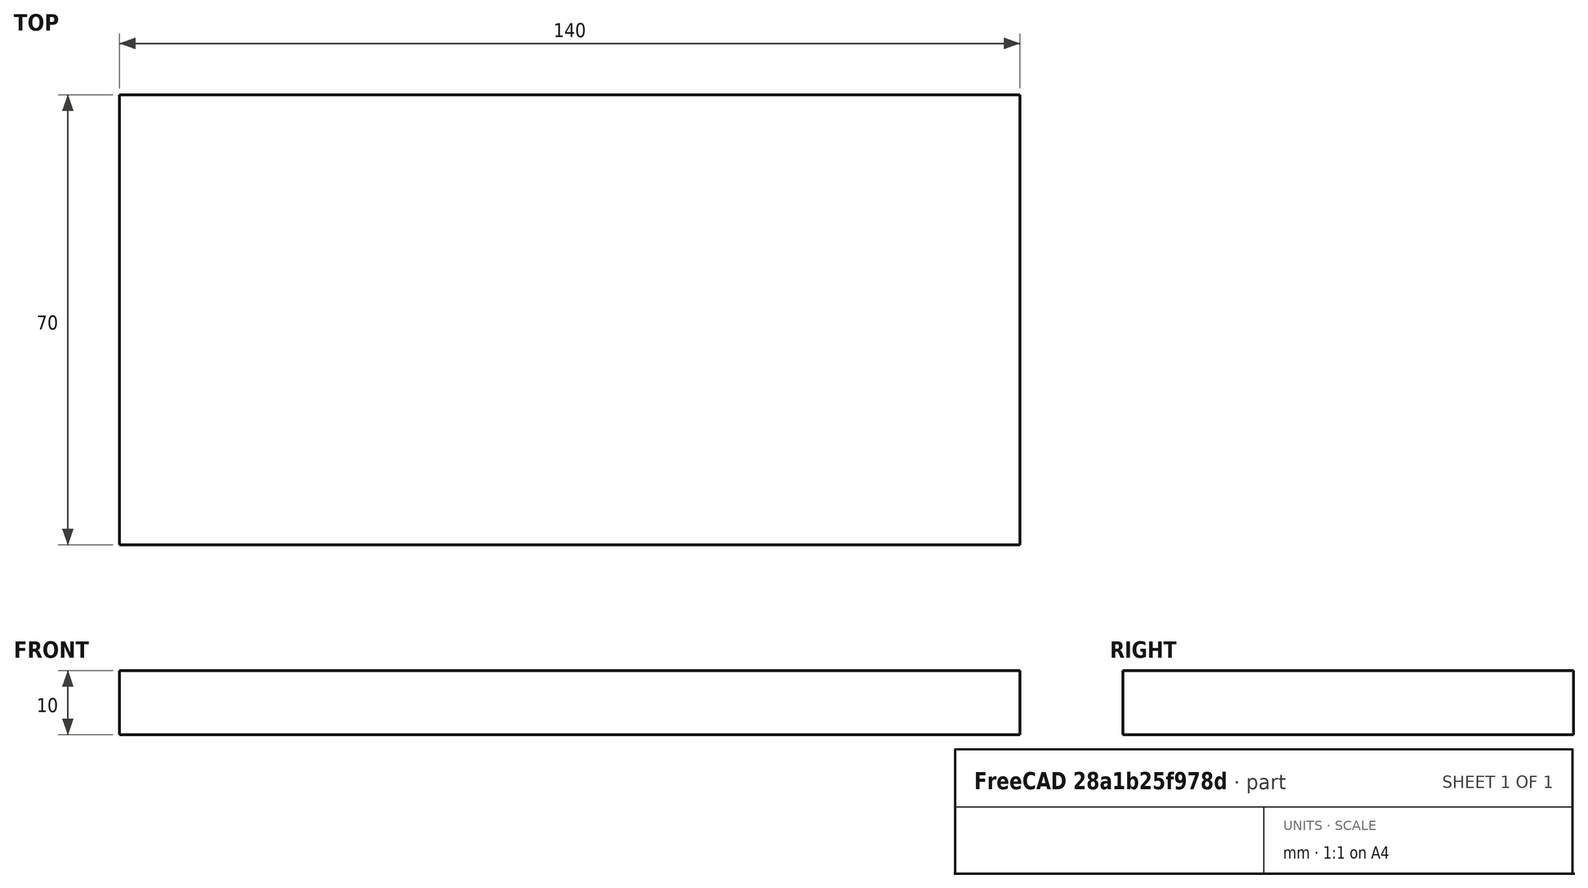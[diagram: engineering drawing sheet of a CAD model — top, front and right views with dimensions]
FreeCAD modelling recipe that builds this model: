
FCSTD DOCUMENT  (FreeCAD 0.18R16093 (Git))
Label: sidePanelRight
License: All rights reserved
LicenseURL: http://en.wikipedia.org/wiki/All_rights_reserved
objects: PartDesign::Fillet×4, Sketcher::SketchObject×3, Path::FeaturePython×3, PartDesign::Pocket×2, Part::FeaturePython×2, PartDesign::Pad×1, PartDesign::Body×1, App::FeaturePython×1, App::DocumentObjectGroup×1, Path::FeatureCompoundPython×1, Mesh::FeaturePython×1
note: 17 computed .brp shape members not serialized (recipe doc carries the construction recipe); baked Part::Feature solids carry a one-line shape summary decoded from their .brp

FEATURE [Sketcher::SketchObject] Sketch
  MapMode = 5
  Placement = pos=(0,0,0) rot=(0.57735,0.57735,0.57735;2.0944rad)
  Support = -> [YZ_Plane]
  sketch-geometry (4):
    g0: LineSegment StartX=-35 StartY=70 StartZ=0 EndX=35 EndY=70 EndZ=0
    g1: LineSegment StartX=35 StartY=70 StartZ=0 EndX=35 EndY=-70 EndZ=0
    g2: LineSegment StartX=35 StartY=-70 StartZ=0 EndX=-35 EndY=-70 EndZ=0
    g3: LineSegment StartX=-35 StartY=-70 StartZ=0 EndX=-35 EndY=70 EndZ=0
  constraints (10):
    c: Coincident(g0,g1)
    c: Coincident(g1,g2)
    c: Coincident(g2,g3)
    c: Coincident(g3,g0)
    c: DistanceY(g3,g3) = 140
    c: DistanceX(g0,g0) = 70
    c: Symmetric(g0,g0,g-2)
    c: Symmetric(g0,g2,g-1)
    c: Parallel(g3,g1)
    c: Parallel(g0,g2)
FEATURE [PartDesign::Pad] Pad
  Length = 10
  Length2 = 100
  Placement = pos=(0,0,0) rot=(0.57735,0.57735,0.57735;2.0944rad)
  Profile = -> Sketch
  Type = 0
FEATURE [PartDesign::Fillet] Fillet
  Base = -> Pad [Edge4]
  BaseFeature = -> Pad
  Placement = pos=(0,0,0) rot=(0.57735,0.57735,0.57735;2.0944rad)
  Radius = 3
FEATURE [PartDesign::Fillet] Fillet001
  Base = -> Fillet [Edge15]
  BaseFeature = -> Fillet
  Placement = pos=(0,0,0) rot=(0.57735,0.57735,0.57735;2.0944rad)
  Radius = 3
FEATURE [Sketcher::SketchObject] Sketch001
  MapMode = 5
  Placement = pos=(0,0,0) rot=(0.57735,0.57735,-0.57735;4.18879rad)
  Support = -> [Fillet001]
  sketch-geometry (24):
    g0: LineSegment StartX=-25 StartY=70 StartZ=0 EndX=-15 EndY=70 EndZ=0
    g1: LineSegment StartX=-15 StartY=70 StartZ=0 EndX=-15 EndY=60 EndZ=0
    g2: LineSegment StartX=-15 StartY=60 StartZ=0 EndX=-25 EndY=60 EndZ=0
    g3: LineSegment StartX=-25 StartY=60 StartZ=0 EndX=-25 EndY=70 EndZ=0
    g4: LineSegment StartX=-5 StartY=70 StartZ=0 EndX=5 EndY=70 EndZ=0
    g5: LineSegment StartX=5 StartY=70 StartZ=0 EndX=5 EndY=60 EndZ=0
    g6: LineSegment StartX=5 StartY=60 StartZ=0 EndX=-5 EndY=60 EndZ=0
    g7: LineSegment StartX=-5 StartY=60 StartZ=0 EndX=-5 EndY=70 EndZ=0
    g8: LineSegment StartX=25 StartY=70 StartZ=0 EndX=15 EndY=70 EndZ=0
    g9: LineSegment StartX=15 StartY=70 StartZ=0 EndX=15 EndY=60 EndZ=0
    g10: LineSegment StartX=15 StartY=60 StartZ=0 EndX=25 EndY=60 EndZ=0
    g11: LineSegment StartX=25 StartY=60 StartZ=0 EndX=25 EndY=70 EndZ=0
    g12: LineSegment StartX=-25 StartY=-70 StartZ=0 EndX=-15 EndY=-70 EndZ=0
    g13: LineSegment StartX=-15 StartY=-70 StartZ=0 EndX=-15 EndY=-60 EndZ=0
    g14: LineSegment StartX=-15 StartY=-60 StartZ=0 EndX=-25 EndY=-60 EndZ=0
    g15: LineSegment StartX=-25 StartY=-60 StartZ=0 EndX=-25 EndY=-70 EndZ=0
    g16: LineSegment StartX=-5 StartY=-70 StartZ=0 EndX=5 EndY=-70 EndZ=0
    g17: LineSegment StartX=5 StartY=-70 StartZ=0 EndX=5 EndY=-60 EndZ=0
    g18: LineSegment StartX=5 StartY=-60 StartZ=0 EndX=-5 EndY=-60 EndZ=0
    g19: LineSegment StartX=-5 StartY=-60 StartZ=0 EndX=-5 EndY=-70 EndZ=0
    g20: LineSegment StartX=25 StartY=-70 StartZ=0 EndX=15 EndY=-70 EndZ=0
    g21: LineSegment StartX=15 StartY=-70 StartZ=0 EndX=15 EndY=-60 EndZ=0
    g22: LineSegment StartX=15 StartY=-60 StartZ=0 EndX=25 EndY=-60 EndZ=0
    g23: LineSegment StartX=25 StartY=-60 StartZ=0 EndX=25 EndY=-70 EndZ=0
  constraints (70):
    c: Coincident(g0,g1)
    c: Coincident(g1,g2)
    c: Coincident(g2,g3)
    c: Coincident(g3,g0)
    c: Horizontal(g0)
    c: Horizontal(g2)
    c: Vertical(g1)
    c: Vertical(g3)
    c: DistanceX(g0,g0) = 10
    c: DistanceY(g2,g0) = 10
    c: DistanceY(g-1,g2) = 60
    c: Coincident(g4,g5)
    c: Coincident(g5,g6)
    c: Coincident(g6,g7)
    c: Coincident(g7,g4)
    c: Horizontal(g6)
    c: Vertical(g5)
    c: Vertical(g7)
    c: DistanceX(g0,g4) = 10
    c: DistanceX(g4,g4) = 10
    c: Horizontal(g6,g1)
    c: Horizontal(g4,g0)
    c: Coincident(g8,g9)
    c: Coincident(g9,g10)
    c: Coincident(g10,g11)
    c: Coincident(g11,g8)
    c: Horizontal(g8)
    c: Horizontal(g10)
    c: Vertical(g9)
    c: Vertical(g11)
    c: Horizontal(g5,g9)
    c: Horizontal(g4,g8)
    c: DistanceX(g4,g8) = 10
    c: DistanceX(g8,g8) = 10
    c: Coincident(g12,g13)
    c: Coincident(g13,g14)
    c: Coincident(g14,g15)
    c: Coincident(g15,g12)
    c: Horizontal(g12)
    c: Horizontal(g14)
    c: Vertical(g13)
    c: Vertical(g15)
    c: Coincident(g16,g17)
    c: Coincident(g17,g18)
    c: Coincident(g18,g19)
    c: Coincident(g19,g16)
    c: Horizontal(g16)
    c: Vertical(g17)
    c: Vertical(g19)
    c: Coincident(g20,g21)
    c: Coincident(g21,g22)
    c: Coincident(g22,g23)
    c: Coincident(g23,g20)
    c: Horizontal(g20)
    c: Horizontal(g22)
    c: Vertical(g21)
    c: Vertical(g23)
    c: DistanceY(g14,g-1) = 60
    c: DistanceY(g12,g14) = 10
    c: Horizontal(g13,g18)
    c: Horizontal(g17,g21)
    c: Horizontal(g12,g16)
    c: Horizontal(g16,g20)
    c: DistanceX(g12,g12) = 10
    c: DistanceX(g12,g16) = 10
    c: DistanceX(g16,g16) = 10
    c: DistanceX(g16,g20) = 10
    c: DistanceX(g20,g20) = 10
    c: Symmetric(g18,g17,g-2)
    c: Symmetric(g4,g4,g-2)
FEATURE [PartDesign::Pocket] Pocket
  BaseFeature = -> Fillet001
  Length = 5
  Length2 = 100
  Placement = pos=(0,0,0) rot=(0.57735,0.57735,0.57735;2.0944rad)
  Profile = -> Sketch001
  Type = 1
FEATURE [Sketcher::SketchObject] Sketch002
  MapMode = 5
  Placement = pos=(0,0,0) rot=(0.57735,0.57735,-0.57735;4.18879rad)
  Support = -> [Pocket]
  sketch-geometry (8):
    g0: ArcOfCircle CenterX=27.5 CenterY=-65 CenterZ=0 NormalX=0 NormalY=0 NormalZ=1 AngleXU=0 Radius=2.5 StartAngle=3.14159 EndAngle=6.28319
    g1: ArcOfCircle CenterX=27.5 CenterY=65 CenterZ=0 NormalX=0 NormalY=0 NormalZ=1 AngleXU=0 Radius=2.5 StartAngle=0 EndAngle=3.14159
    g2: LineSegment StartX=30 StartY=-65 StartZ=0 EndX=30 EndY=65 EndZ=0
    g3: LineSegment StartX=25 StartY=-65 StartZ=0 EndX=25 EndY=65 EndZ=0
    g4: ArcOfCircle CenterX=-27.5 CenterY=-70 CenterZ=0 NormalX=0 NormalY=0 NormalZ=1 AngleXU=0 Radius=2.5 StartAngle=3.14159 EndAngle=6.28319
    g5: ArcOfCircle CenterX=-27.5 CenterY=65 CenterZ=0 NormalX=0 NormalY=0 NormalZ=1 AngleXU=0 Radius=2.5 StartAngle=0 EndAngle=3.14159
    g6: LineSegment StartX=-25 StartY=-70 StartZ=0 EndX=-25 EndY=65 EndZ=0
    g7: LineSegment StartX=-30 StartY=-70 StartZ=0 EndX=-30 EndY=65 EndZ=0
  constraints (20):
    c: Tangent(g0,g3) = 1.5708
    c: Tangent(g0,g2) = -1.5708
    c: Tangent(g2,g1) = -1.5708
    c: Tangent(g3,g1) = 1.5708
    c: Vertical(g2)
    c: Equal(g0,g1)
    c: Tangent(g4,g7) = 1.5708
    c: Tangent(g4,g6) = -1.5708
    c: Tangent(g6,g5) = -1.5708
    c: Tangent(g7,g5) = 1.5708
    c: Vertical(g6)
    c: Equal(g4,g5)
    c: Radius(g1) = 2.5
    c: Radius(g4) = 2.5
    c: DistanceX(g-1,g0) = 25
    c: DistanceX(g4,g-1) = 25
    c: DistanceY(g0,g1) = 130
    c: DistanceY(g4,g5) = 135
    c: DistanceY(g-1,g5) = 65
    c: Horizontal(g1,g5)
FEATURE [PartDesign::Pocket] Pocket001
  BaseFeature = -> Pocket
  Length = 5
  Length2 = 100
  Placement = pos=(0,0,0) rot=(0.57735,0.57735,0.57735;2.0944rad)
  Profile = -> Sketch002
  Type = 0
FEATURE [PartDesign::Fillet] Fillet002
  Base = -> Pocket001 [Edge1]
  BaseFeature = -> Pocket001
  Placement = pos=(0,0,0) rot=(0.57735,0.57735,0.57735;2.0944rad)
  Radius = 3
FEATURE [PartDesign::Fillet] Fillet003
  Base = -> Fillet002 [Edge61]
  BaseFeature = -> Fillet002
  Placement = pos=(0,0,0) rot=(0.57735,0.57735,0.57735;2.0944rad)
  Radius = 3
FEATURE [PartDesign::Body] Body  label="SidePanelRight"
  Group = -> [Sketch,Pad,Fillet,Fillet001,Sketch001,Pocket,Sketch002,Pocket001,Fillet002,Fillet003]
  Origin = -> Origin
  Placement = pos=(0,0,0) rot=(0,1,0;1.5708rad)
  Tip = -> Fillet003
FEATURE [App::FeaturePython] SetupSheet  # Path/CAM operation (typed FeaturePython)
  ClearanceHeightExpression = OpStockZMax+SetupSheet.ClearanceHeightOffset
  ClearanceHeightOffset = 5
  FinalDepthExpression = OpFinalDepth
  HorizRapid = 0
  SafeHeightExpression = OpStockZMax+SetupSheet.SafeHeightOffset
  SafeHeightOffset = 3
  StartDepthExpression = OpStartDepth
  StepDownExpression = OpToolDiameter
  VertRapid = 0
FEATURE [Part::FeaturePython] Clone  label="Model-SidePanelRight"  # Draft clone (typed FeaturePython)
  AttacherType = Attacher::AttachEngine3D
  Fuse = false
  Objects = -> [Body]
  PathResource = Model
  Placement = pos=(70,35,-1.16653e-11) rot=(0,1,0;1.5708rad)
  Scale = (1,1,1)
FEATURE [App::DocumentObjectGroup] Model
  Group = -> [Clone]
FEATURE [Path::FeaturePython] Default_Tool  label="stealWood5mm"  # Path/CAM operation (typed FeaturePython)
  HorizFeed = 5000
  HorizRapid = 0
  SpindleDir = 0
  SpindleSpeed = 10000
  ToolNumber = 1
  VertFeed = 500
  VertRapid = 0
  expr: HorizRapid = SetupSheet.HorizRapid
  expr: VertRapid = SetupSheet.VertRapid
FEATURE [Part::FeaturePython] Stock  # WARN: FeaturePython — macro-defined, semantics opaque (R4)
  Base = -> Model
  ExtXneg = 0
  ExtXpos = 0
  ExtYneg = 0
  ExtYpos = 0
  ExtZneg = 0
  ExtZpos = 0
  Placement = pos=(0,0,-10) rot=(0,0,1;0rad)
  StockType = FromBase
FEATURE [Path::FeaturePython] Pocket_Shape  # Path/CAM operation (typed FeaturePython)
  Active = true
  AreaParams:
    Tolerance = 1e-07
    FitArcs = True
    Simplify = False
    CleanDistance = 0.0
    Accuracy = 0.01
    Unit = 1.0
    MinArcPoints = 4
    MaxArcPoints = 100
    ClipperScale = 10000000.0
    Fill = 0
    Coplanar = 0
    Reorient = True
    Outline = False
    Explode = False
    OpenMode = 0
    Deflection = 0.01
    SubjectFill = 0
    ClipFill = 0
    Offset = 0.0
    ExtraPass = 0
    Stepover = 0.0
    LastStepover = 0.0
    JoinType = 0
    EndType = 0
    MiterLimit = 2.0
    RoundPrecision = 0.0
    PocketMode = 1
    ToolRadius = 2.495
    PocketExtraOffset = 0.0
    PocketStepover = 4.99
    PocketLastStepover = 0.0
    FromCenter = True
    Angle = 45.0
    AngleShift = 0.0
    Shift = 0.0
    Thicken = False
    SectionCount = -1
    Stepdown = 1.0
    SectionOffset = 0.0
    SectionTolerance = 1e-06
    SectionMode = 2
    Project = False
  Base = -> [Clone]
  ClearanceHeight = 5
  CutMode = 0
  ExtraOffset = 0
  FinalDepth = -5
  FinishDepth = 0
  KeepToolDown = false
  MinTravel = false
  OffsetPattern = 0
  OpFinalDepth = -5
  OpStartDepth = 6e-16
  OpStockZMax = -1.8e-15
  OpStockZMin = -10
  OpToolDiameter = 4.99
  PathParams = {'orientation': 1, 'feedrate': 5000.0, 'feedrate_v': 500.0, 'verbose': True, 'resume_height': 2.9999999999999982, 'retraction': 4.999999999999998, 'return_end': True, 'preamble': False}
  SafeHeight = 3
  StartAt = 0
  StartDepth = 6e-16
  StartPoint = (0,0,0)
  StepDown = 4.99
  StepOver = 100
  ToolController = -> Default_Tool
  UseOutline = false
  UseStartPoint = false
  ZigZagAngle = 45
  expr: ClearanceHeight = OpStockZMax + SetupSheet.ClearanceHeightOffset
  expr: SafeHeight = OpStockZMax + SetupSheet.SafeHeightOffset
  expr: StepDown = OpToolDiameter
  expr: FinalDepth = OpFinalDepth
  expr: StartDepth = OpStartDepth
FEATURE [Path::FeatureCompoundPython] Operations  # Path/CAM operation (typed FeaturePython)
  Group = -> [Pocket_Shape]
  UsePlacements = false
FEATURE [Path::FeaturePython] Job  # Path/CAM operation (typed FeaturePython)
  GeometryTolerance = 0.01
  Model = -> Model
  Operations = -> Operations
  PostProcessor = 1
  SetupSheet = -> SetupSheet
  Stock = -> Stock
  ToolController = -> [Default_Tool]
FEATURE [Mesh::FeaturePython] CutMaterial  # WARN: FeaturePython — macro-defined, semantics opaque (R4)
